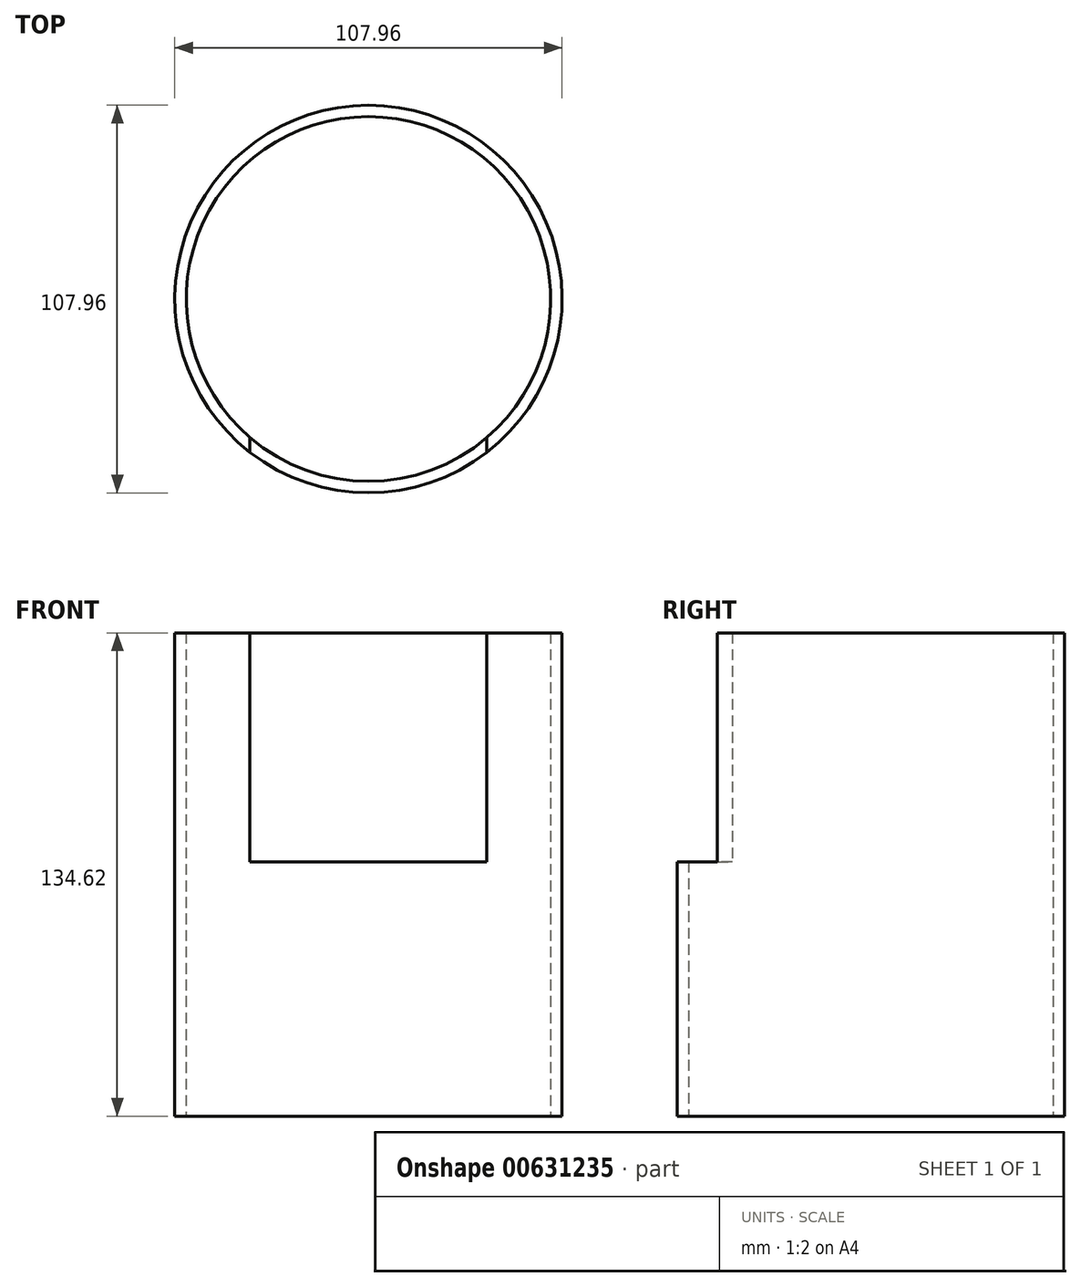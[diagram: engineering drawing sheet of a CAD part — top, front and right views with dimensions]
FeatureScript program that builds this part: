
annotation { "Feature Type Name" : "Feature", "Feature Type Description" : "" }
export const myFeature = defineFeature(function(context is Context, id is Id, definition is map)
    precondition{}
    {
        {
            var Q0;
            Q0=qCreatedBy(makeId("Top.planeOp"),FACE);
            var sketch = newSketch(context, id + "F0", { "sketchPlane" : qUnion([Q0])});
            skCircle(sketch, "E0", {"center": v(0, 0) * mm, "radius": 50.8 * mm});
            skCircle(sketch, "E1", {"center": v(0, 0) * mm, "radius": 53.98 * mm});
            skSolve(sketch);
        }
        {
            var Q0;
            Q0 = qSketchRegion(id + "F0", true);
            extrude(context, id + "F1", {"entities" : qUnion([Q0]), "depth" : 134.62 * mm, "offsetDistance" : 25.4 * mm});
        }
        {
            var Q0;
            Q0=qCreatedBy(makeId("Front.planeOp"),FACE);
            var sketch = newSketch(context, id + "F2", { "sketchPlane" : qUnion([Q0])});
            skLineSegment(sketch, "E2.bottom", {"start": v(33.02, 70.85) * mm, "end": v(-33.02, 70.85) * mm});
            skLineSegment(sketch, "E2.top", {"start": v(33.02, 197.85) * mm, "end": v(-33.02, 197.85) * mm});
            skLineSegment(sketch, "E2.left", {"start": v(33.02, 70.85) * mm, "end": v(33.02, 197.85) * mm});
            skLineSegment(sketch, "E2.right", {"start": v(-33.02, 70.85) * mm, "end": v(-33.02, 197.85) * mm});
            skPoint(sketch, "E2.middle", {"position": v(0, 134.35) * mm});
            skSolve(sketch);
        }
        {
            var Q0;
            Q0=makeQuery(id+"F2.imprint","IMPRINT",FACE,{"disambiguationData":[TD([[makeQuery(id+"F2.imprint","IMPRINT",EDGE,{"derivedFrom":sQuery(id+"F2.wireOp",EDGE,"E2.bottom")}),-1.0]])]});
            extrude(context, id + "F3", {"entities" : qUnion([Q0]), "operationType" : NewBodyOperationType.REMOVE, "depth" : 89.66 * mm, "offsetDistance" : 25.4 * mm});
        }
    });
